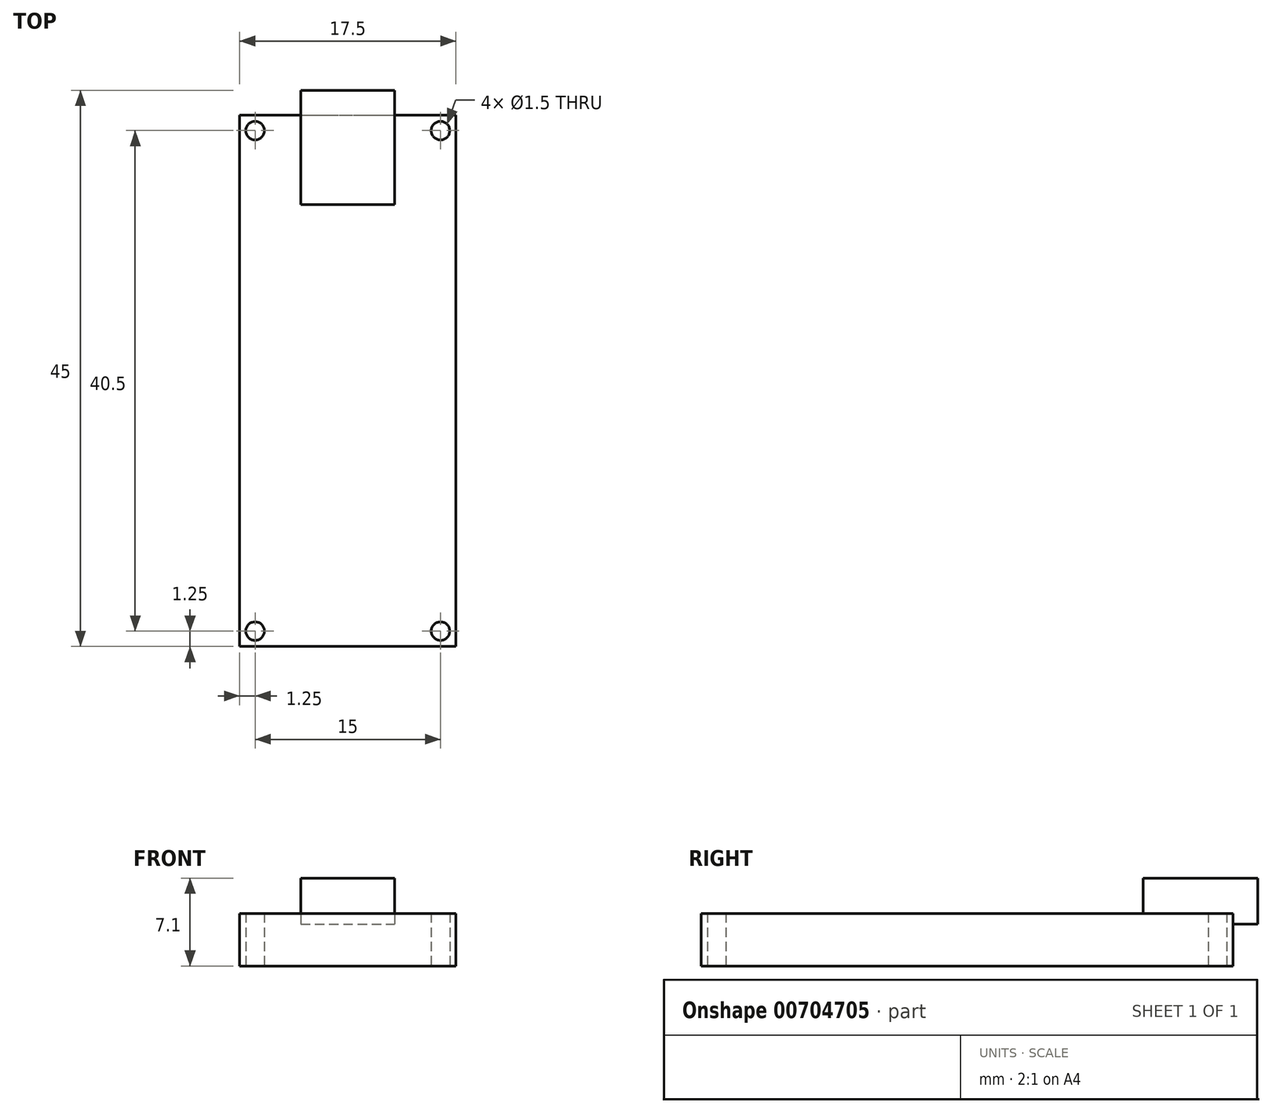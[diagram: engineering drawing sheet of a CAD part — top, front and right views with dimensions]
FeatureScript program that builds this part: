
annotation { "Feature Type Name" : "Feature", "Feature Type Description" : "" }
export const myFeature = defineFeature(function(context is Context, id is Id, definition is map)
    precondition{}
    {
        {
            var Q0;
            Q0=qCreatedBy(makeId("Top.planeOp"),FACE);
            var sketch = newSketch(context, id + "F0", { "sketchPlane" : qUnion([Q0])});
            skLineSegment(sketch, "E0.bottom", {"start": v(-8.75, 21.5) * mm, "end": v(8.75, 21.5) * mm});
            skLineSegment(sketch, "E0.top", {"start": v(-8.75, -21.5) * mm, "end": v(8.75, -21.5) * mm});
            skLineSegment(sketch, "E0.left", {"start": v(-8.75, 21.5) * mm, "end": v(-8.75, -21.5) * mm});
            skLineSegment(sketch, "E0.right", {"start": v(8.75, 21.5) * mm, "end": v(8.75, -21.5) * mm});
            skLineSegment(sketch, "E1.bottom", {"start": v(-3.8, 23.5) * mm, "end": v(3.8, 23.5) * mm});
            skLineSegment(sketch, "E1.top", {"start": v(-3.8, 14.25) * mm, "end": v(3.8, 14.25) * mm});
            skLineSegment(sketch, "E1.left", {"start": v(-3.8, 23.5) * mm, "end": v(-3.8, 14.25) * mm});
            skLineSegment(sketch, "E1.right", {"start": v(3.8, 23.5) * mm, "end": v(3.8, 14.25) * mm});
            skCircle(sketch, "E2", {"center": v(7.5, 20.25) * mm, "radius": 0.75 * mm});
            skCircle(sketch, "E3", {"center": v(-7.5, 20.25) * mm, "radius": 0.75 * mm});
            skCircle(sketch, "E4", {"center": v(7.5, -20.25) * mm, "radius": 0.75 * mm});
            skCircle(sketch, "E5", {"center": v(-7.5, -20.25) * mm, "radius": 0.75 * mm});
            skSolve(sketch);
        }
        {
            var Q0;
            Q0=makeQuery(id+"F0.imprint","IMPRINT",FACE,{"disambiguationData":[TD([[makeQuery(id+"F0.imprint","IMPRINT",EDGE,{"derivedFrom":sQuery(id+"F0.wireOp",EDGE,"E0.top")}),1.0]])]});
            var Q1;
            {var subQ5=sQuery(id+"F0.wireOp",EDGE,"E1.top");Q1=makeQuery(id+"F0.imprint","IMPRINT",FACE,{"disambiguationData":[TD([[makeQuery(id+"F0.imprint","IMPRINT",EDGE,{"derivedFrom":subQ5}),1.0]])]});}
            extrude(context, id + "F1", {"entities" : qUnion([Q0, Q1]), "depth" : 4.25 * mm, "offsetDistance" : 25 * mm});
        }
        {
            var Q0;
            {var subQ5=sQuery(id+"F0.wireOp",EDGE,"E1.top");Q0=makeQuery(id+"F0.imprint","IMPRINT",FACE,{"disambiguationData":[TD([[makeQuery(id+"F0.imprint","IMPRINT",EDGE,{"derivedFrom":subQ5}),1.0]])]});}
            var Q1;
            {var subQ5=sQuery(id+"F0.wireOp",EDGE,"E1.bottom");Q1=makeQuery(id+"F0.imprint","IMPRINT",FACE,{"disambiguationData":[TD([[makeQuery(id+"F0.imprint","IMPRINT",EDGE,{"derivedFrom":subQ5}),-1.0]])]});}
            extrude(context, id + "F2", {"entities" : qUnion([Q0, Q1]), "operationType" : NewBodyOperationType.ADD, "depth" : 7.1 * mm, "offsetDistance" : 25 * mm, "hasSecondDirection" : true, "secondDirectionOppositeDirection" : false, "secondDirectionDepth" : 3.4 * mm});
        }
    });
